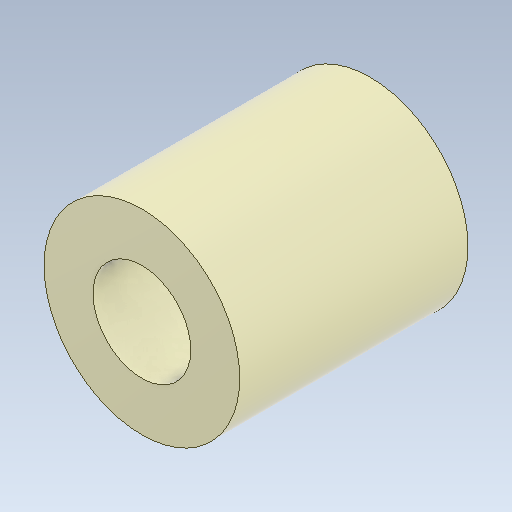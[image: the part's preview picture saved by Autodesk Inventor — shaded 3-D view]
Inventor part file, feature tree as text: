
AUTODESK INVENTOR PART (.ipt)
format: ipt  version: 2020.2 (Build 242310000, 310)  size: 110,592 bytes
history: native  units: mm
features: other x1, extrude x1, sketch x1
ambient origin geometry x8: Origin, YZ Plane, XZ Plane, XY Plane, X Axis, Y Axis, Z Axis, Center Point
bodies: Body1 (feature_tree)
feature tree (3):
  other  "ソリッド1"
  extrude  "押し出し1"  Depth=6.0mm
  sketch  "スケッチ1"
